annotation { "Feature Type Name" : "Feature", "Feature Type Description" : "" }
export const myFeature = defineFeature(function(context is Context, id is Id, definition is map)
    precondition{}
    {
        {
            var Q0;
            Q0=qCreatedBy(makeId("Front.planeOp"),FACE);
            var sketch = newSketch(context, id + "F0", { "sketchPlane" : qUnion([Q0])});
            skLineSegment(sketch, "E0.bottom", {"start": v(0, 0) * mm, "end": v(300, 0) * mm, "construction": true});
            skLineSegment(sketch, "E0.top", {"start": v(0, 200) * mm, "end": v(300, 200) * mm, "construction": true});
            skLineSegment(sketch, "E0.left", {"start": v(0, 0) * mm, "end": v(0, 200) * mm, "construction": true});
            skLineSegment(sketch, "E0.right", {"start": v(300, 0) * mm, "end": v(300, 200) * mm, "construction": true});
            skLineSegment(sketch, "E1", {"start": v(0, 39.97) * mm, "end": v(300, 39.97) * mm});
            skText(sketch, "E2", { "text": "TAJ MAHAL", "fontName": "OpenSans-Italic.ttf"});
            skLineSegment(sketch, "E3", {"start": v(0, 54.75) * mm, "end": v(300, 54.75) * mm});
            skLineSegment(sketch, "E4", {"start": v(297.37, 54.75) * mm, "end": v(293.4, 169.68) * mm});
            skLineSegment(sketch, "E5", {"start": v(293.4, 169.68) * mm, "end": v(297.37, 54.75) * mm});
            skLineSegment(sketch, "E6", {"start": v(275.67, 54.75) * mm, "end": v(279.12, 169.68) * mm});
            skLineSegment(sketch, "E7", {"start": v(279.12, 169.68) * mm, "end": v(293.4, 169.68) * mm});
            skLineSegment(sketch, "E8", {"start": v(28.92, 54.68) * mm, "end": v(24.95, 169.61) * mm});
            skLineSegment(sketch, "E9", {"start": v(24.95, 169.61) * mm, "end": v(28.92, 54.68) * mm});
            skLineSegment(sketch, "E10", {"start": v(7.23, 54.68) * mm, "end": v(10.67, 169.61) * mm});
            skLineSegment(sketch, "E11", {"start": v(10.67, 169.61) * mm, "end": v(24.95, 169.61) * mm});
            skLineSegment(sketch, "E12", {"start": v(55.48, 54.75) * mm, "end": v(55.48, 105.15) * mm});
            skLineSegment(sketch, "E13", {"start": v(55.48, 105.15) * mm, "end": v(70.71, 105.15) * mm});
            skLineSegment(sketch, "E14", {"start": v(70.71, 105.15) * mm, "end": v(70.71, 109.24) * mm});
            skLineSegment(sketch, "E15", {"start": v(70.71, 109.24) * mm, "end": v(87.8, 109.24) * mm});
            skLineSegment(sketch, "E16", {"start": v(87.8, 109.24) * mm, "end": v(87.8, 115.18) * mm});
            skLineSegment(sketch, "E17", {"start": v(248.27, 54.75) * mm, "end": v(248.27, 105.52) * mm});
            skLineSegment(sketch, "E18", {"start": v(248.27, 105.52) * mm, "end": v(234.9, 105.52) * mm});
            skLineSegment(sketch, "E19", {"start": v(234.9, 105.52) * mm, "end": v(234.9, 108.87) * mm});
            skLineSegment(sketch, "E20", {"start": v(234.9, 108.87) * mm, "end": v(215.6, 109.44) * mm});
            skLineSegment(sketch, "E21", {"start": v(215.6, 109.44) * mm, "end": v(215.6, 114.8) * mm});
            skArc(sketch, "E22", {"start": v(215.6, 114.8) * mm, "mid": v(151.87, 173.06) * mm, "end": v(87.8, 115.18) * mm});
            skLineSegment(sketch, "E23", {"start": v(147.22, 172.9) * mm, "end": v(147.22, 190.59) * mm});
            skLineSegment(sketch, "E24", {"start": v(147.22, 190.59) * mm, "end": v(151.69, 190.59) * mm});
            skLineSegment(sketch, "E25", {"start": v(151.69, 190.59) * mm, "end": v(151.69, 173.06) * mm});
            skArc(sketch, "E26", {"start": v(24.95, 169.61) * mm, "mid": v(17.81, 184.15) * mm, "end": v(10.67, 169.61) * mm});
            skArc(sketch, "E27", {"start": v(293.4, 169.68) * mm, "mid": v(286.26, 184.84) * mm, "end": v(279.12, 169.68) * mm});
            skArc(sketch, "E28", {"start": v(87.8, 115.18) * mm, "mid": v(75.07, 124.23) * mm, "end": v(70.71, 109.24) * mm});
            skArc(sketch, "E29", {"start": v(234.9, 108.87) * mm, "mid": v(229.27, 124.9) * mm, "end": v(215.6, 114.8) * mm});
            const initialGuessF0  = {"E2": [0.04916, 0.00389, 1, 0, 0.03086]};
            skSetInitialGuess(sketch, initialGuessF0);
            skSolve(sketch);
        }
        {
            var Q0;
            Q0 = qSketchRegion(id + "F0", true);
            extrude(context, id + "F1", {"entities" : qUnion([Q0]), "depth" : 25 * mm, "offsetDistance" : 25 * mm});
        }
    });